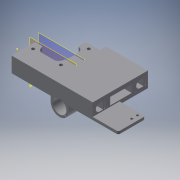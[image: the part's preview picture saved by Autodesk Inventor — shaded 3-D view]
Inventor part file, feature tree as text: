
AUTODESK INVENTOR PART (.ipt)
format: ipt  version: 2016 (Build 200138000, 138)  size: 3,027,968 bytes
history: native  units: mm
features: sketch x9, extrude x6, other x5, projected_geometry x5, hole x2, plane x2, direct_edit x1, mirror x1, imported_body x1, move_body x1
ambient origin geometry x8: Origin, YZ Plane, XZ Plane, XY Plane, X Axis, Y Axis, Z Axis, Center Point
bodies: Solid1 (feature_tree), Solid2 (feature_tree)
feature tree (33):
  other  "z_right_printer_1"
  other  "MeshFeature1"
  direct_edit  "Direct Edit1"
  sketch  "Sketch1"  dims[d0=0.0mm d1=0.0mm d2=5.5mm]
  other  "Work Point1"
  hole  "Hole1"  [1 undecoded]
  extrude  "Extrusion1"  Depth=16.0mm
  hole  "Hole2"  [1 undecoded]
  sketch  "Sketch5"  dims[d14=3.2mm d15=6.0mm d16=4.0mm d17=2.0mm d18=90.0deg d19=23.5mm d20=20.594885mm d21=1.0mm]
  extrude  "Extrusion2"  Depth=1.0mm TaperAngle=0.0deg
  extrude  "Extrusion3"  [1 undecoded]
  plane  "Work Plane1"
  plane  "Work Plane2"
  extrude  "Extrusion4"  Depth=27.0mm TaperAngle=0.0deg
  mirror  "Mirror1"
  extrude  "Extrusion5"  [1 undecoded]
  extrude  "Extrusion6"  [1 undecoded]
  imported_body  "Base2"
  projected_geometry  "Projected Loop1"
  sketch  "Sketch3"  dims[d3=10.8mm d4=6.0mm d5=4.0mm d6=2.0mm d7=90.0deg d8=8.0mm d9=20.594885mm d10=16.0mm]
  projected_geometry  "Projected Loop3"
  sketch  "Sketch4"  dims[d11=10.0mm d12=0.0mm d13=16.0mm]
  sketch  "Sketch6"  dims[d22=1.0mm d23=0.0mm d24=1.0mm d25=0.0mm]
  sketch  "Sketch7"  dims[d26=-26.0mm d27=-26.0mm]
  projected_geometry  "Projected Loop5"
  projected_geometry  "Projected Loop6"
  sketch  "Sketch8"  dims[d28=7.5mm d29=0.0mm d30=27.0mm d31=0.0mm]
  projected_geometry  "Projected Loop7"
  sketch  "Sketch9"  dims[d32=16.0mm d33=0.0mm]
  sketch  "Sketch10"
  other  "Composite1"
  move_body  "Move1"
  other  "Srf1"
note: 5 required parameter values undecoded (feature->parameter linkage not recoverable at this tier; creation-order binding heuristic only, values carry confidence <= 0.55)
